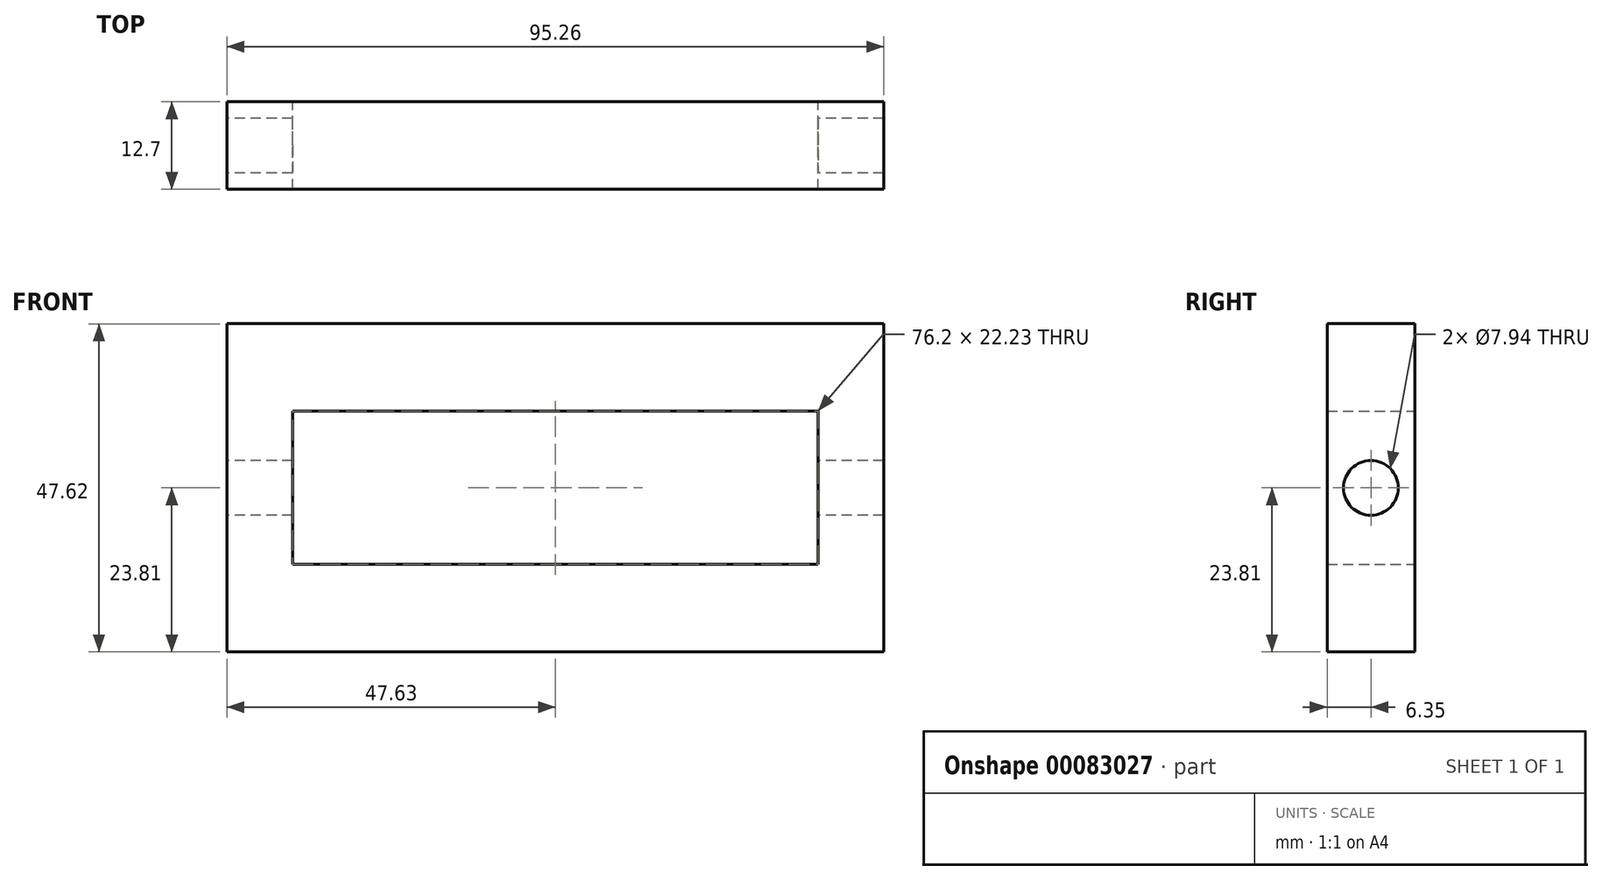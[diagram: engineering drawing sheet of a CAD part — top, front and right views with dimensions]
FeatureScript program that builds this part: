
annotation { "Feature Type Name" : "Feature", "Feature Type Description" : "" }
export const myFeature = defineFeature(function(context is Context, id is Id, definition is map)
    precondition{}
    {
        {
            var Q0;
            Q0=qCreatedBy(makeId("Front.planeOp"),FACE);
            var sketch = newSketch(context, id + "F0", { "sketchPlane" : qUnion([Q0])});
            skLineSegment(sketch, "E0.bottom", {"start": v(-47.62, 23.81) * mm, "end": v(47.63, 23.81) * mm});
            skLineSegment(sketch, "E0.top", {"start": v(-47.63, -23.81) * mm, "end": v(47.62, -23.81) * mm});
            skLineSegment(sketch, "E0.left", {"start": v(-47.62, 23.81) * mm, "end": v(-47.63, -23.81) * mm});
            skLineSegment(sketch, "E0.right", {"start": v(47.63, 23.81) * mm, "end": v(47.62, -23.81) * mm});
            skPoint(sketch, "E0.middle", {"position": v(0, 0) * mm});
            skLineSegment(sketch, "E1.bottom", {"start": v(-38.1, 11.11) * mm, "end": v(38.1, 11.11) * mm});
            skLineSegment(sketch, "E1.top", {"start": v(-38.1, -11.11) * mm, "end": v(38.1, -11.11) * mm});
            skLineSegment(sketch, "E1.left", {"start": v(-38.1, 11.11) * mm, "end": v(-38.1, -11.11) * mm});
            skLineSegment(sketch, "E1.right", {"start": v(38.1, 11.11) * mm, "end": v(38.1, -11.11) * mm});
            skSolve(sketch);
        }
        {
            var Q0;
            Q0=makeQuery(id+"F0.imprint","IMPRINT",FACE,{"disambiguationData":[TD([[makeQuery(id+"F0.imprint","IMPRINT",EDGE,{"derivedFrom":sQuery(id+"F0.wireOp",EDGE,"E0.bottom")}),-1.0]])]});
            extrude(context, id + "F1", {"entities" : qUnion([Q0]), "depth" : 12.7 * mm});
        }
        {
            var Q0;
            Q0=makeQuery(id+"F1.opExtrude","SWEPT_FACE",FACE,{"disambiguationData":[OSD([sQuery(id+"F0.wireOp",EDGE,"E0.left")])]});
            var sketch = newSketch(context, id + "F2", { "sketchPlane" : qUnion([Q0])});
            skCircle(sketch, "E2", {"center": v(6.35, 0) * mm, "radius": 3.97 * mm});
            skPoint(sketch, "E2.centerSnap0", {"position": v(12.7, 0) * mm});
            skSolve(sketch);
        }
        {
            var Q0;
            Q0=makeQuery(id+"F2.imprint","IMPRINT",FACE,{"disambiguationData":[TD([[makeQuery(id+"F2.imprint","IMPRINT",EDGE,{"derivedFrom":sQuery(id+"F2.wireOp",EDGE,"E2")}),1.0]])]});
            extrude(context, id + "F3", {"entities" : qUnion([Q0]), "operationType" : NewBodyOperationType.REMOVE, "endBound" : BoundingType.THROUGH_ALL, "oppositeDirection" : true, "depth" : 25.4 * mm});
        }
    });
